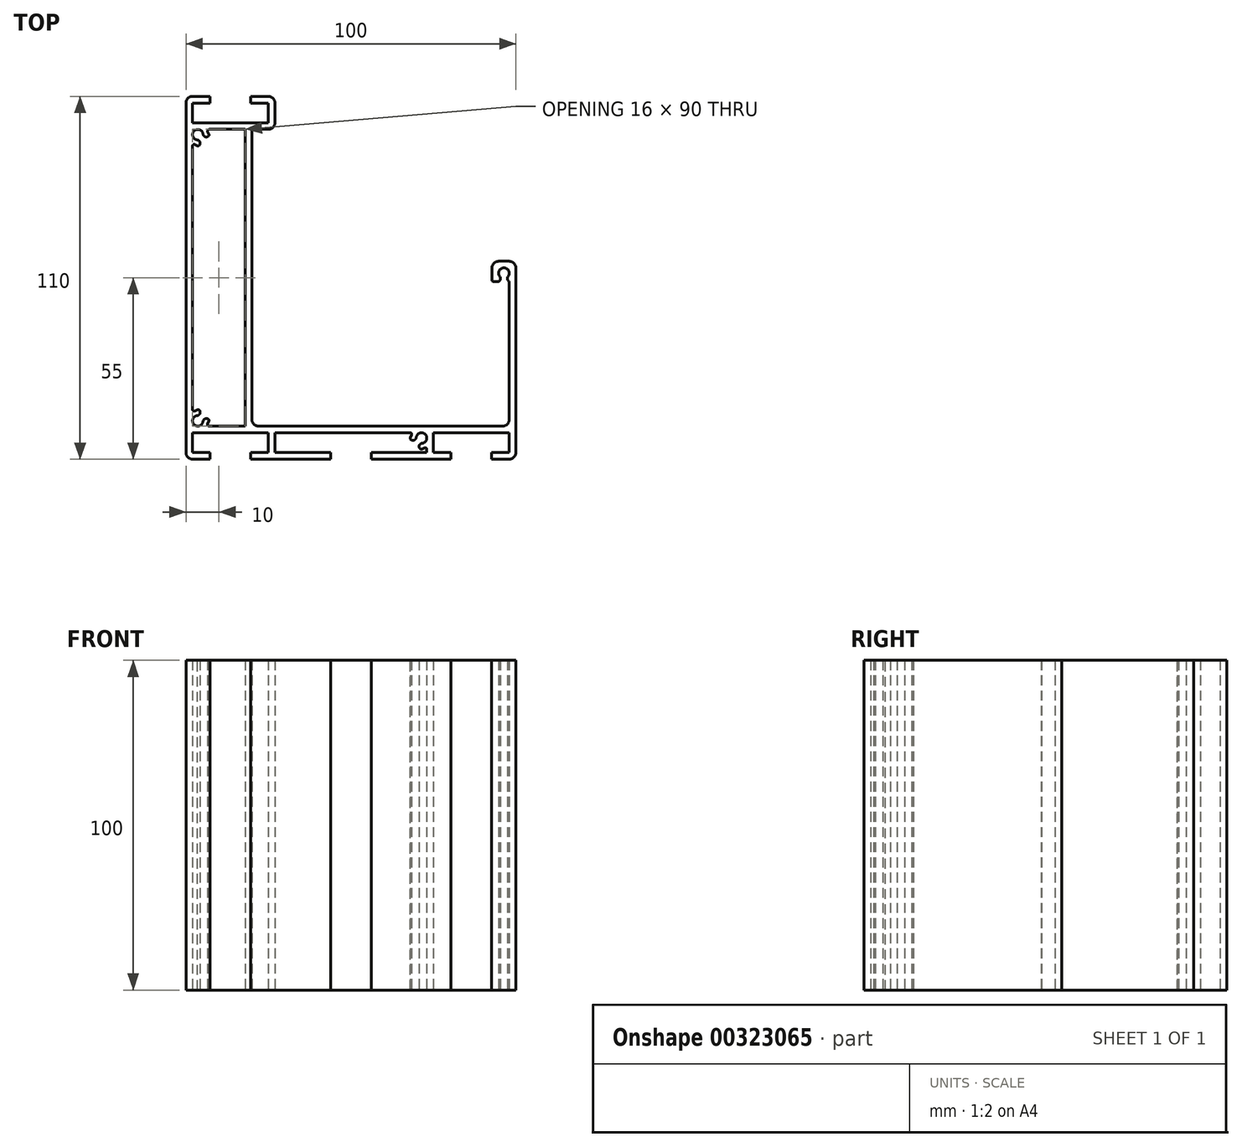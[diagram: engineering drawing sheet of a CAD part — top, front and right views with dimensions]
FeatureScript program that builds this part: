
annotation { "Feature Type Name" : "Feature", "Feature Type Description" : "" }
export const myFeature = defineFeature(function(context is Context, id is Id, definition is map)
    precondition{}
    {
        {
            var Q0;
            Q0=qCreatedBy(makeId("Top.planeOp"),FACE);
            var sketch = newSketch(context, id + "F0", { "sketchPlane" : qUnion([Q0])});
            skLineSegment(sketch, "E0", {"start": v(-2, 108) * mm, "end": v(-2, 2) * mm});
            skArc(sketch, "E1", {"start": v(0, 110) * mm, "mid": v(-1.41, 109.41) * mm, "end": v(-2, 108) * mm});
            skLineSegment(sketch, "E2", {"start": v(0, 108) * mm, "end": v(0, 102) * mm});
            skLineSegment(sketch, "E3", {"start": v(0, 94.94) * mm, "end": v(0, 15.06) * mm});
            skLineSegment(sketch, "E4", {"start": v(0, 8) * mm, "end": v(0, 2) * mm});
            skLineSegment(sketch, "E5", {"start": v(0, 0) * mm, "end": v(5.35, 0) * mm});
            skArc(sketch, "E6", {"start": v(-2, 2) * mm, "mid": v(-1.41, 0.59) * mm, "end": v(0, 0) * mm});
            skLineSegment(sketch, "E7", {"start": v(17.65, 0) * mm, "end": v(41.85, 0) * mm});
            skLineSegment(sketch, "E8", {"start": v(54.15, 0) * mm, "end": v(78.35, 0) * mm});
            skLineSegment(sketch, "E9", {"start": v(90.65, 0) * mm, "end": v(96, 0) * mm});
            skLineSegment(sketch, "E10", {"start": v(0, 2) * mm, "end": v(5.35, 2) * mm});
            skLineSegment(sketch, "E11", {"start": v(17.65, 2) * mm, "end": v(23, 2) * mm});
            skLineSegment(sketch, "E12", {"start": v(25, 2) * mm, "end": v(41.85, 2) * mm});
            skLineSegment(sketch, "E13", {"start": v(54.15, 2) * mm, "end": v(71, 2) * mm});
            skLineSegment(sketch, "E14", {"start": v(73, 2) * mm, "end": v(78.35, 2) * mm});
            skLineSegment(sketch, "E15", {"start": v(90.65, 2) * mm, "end": v(96, 2) * mm});
            skLineSegment(sketch, "E16", {"start": v(98, 2) * mm, "end": v(98, 58) * mm});
            skArc(sketch, "E17", {"start": v(98, 58) * mm, "mid": v(97.41, 59.41) * mm, "end": v(96, 60) * mm});
            skArc(sketch, "E18", {"start": v(96, 0) * mm, "mid": v(97.41, 0.59) * mm, "end": v(98, 2) * mm});
            skLineSegment(sketch, "E19", {"start": v(96, 2) * mm, "end": v(96, 8) * mm});
            skLineSegment(sketch, "E20", {"start": v(96, 12) * mm, "end": v(96, 53.87) * mm});
            skLineSegment(sketch, "E21", {"start": v(90.8, 54.28) * mm, "end": v(90.8, 58) * mm});
            skArc(sketch, "E22", {"start": v(90.8, 54.28) * mm, "mid": v(90.95, 53.92) * mm, "end": v(91.3, 53.78) * mm});
            skArc(sketch, "E23", {"start": v(94, 10) * mm, "mid": v(95.41, 10.59) * mm, "end": v(96, 12) * mm});
            skLineSegment(sketch, "E24", {"start": v(0, 110) * mm, "end": v(5.35, 110) * mm});
            skLineSegment(sketch, "E25", {"start": v(17.65, 110) * mm, "end": v(23, 110) * mm});
            skLineSegment(sketch, "E26", {"start": v(0, 108) * mm, "end": v(5.35, 108) * mm});
            skLineSegment(sketch, "E27", {"start": v(17.65, 108) * mm, "end": v(23, 108) * mm});
            skLineSegment(sketch, "E28", {"start": v(25, 108) * mm, "end": v(25, 102) * mm});
            skArc(sketch, "E29", {"start": v(25, 108) * mm, "mid": v(24.41, 109.41) * mm, "end": v(23, 110) * mm});
            skLineSegment(sketch, "E30", {"start": v(23, 108) * mm, "end": v(23, 102) * mm});
            skLineSegment(sketch, "E31", {"start": v(23, 100) * mm, "end": v(18, 100) * mm});
            skArc(sketch, "E32", {"start": v(23, 100) * mm, "mid": v(24.41, 100.59) * mm, "end": v(25, 102) * mm});
            skLineSegment(sketch, "E33", {"start": v(16, 100) * mm, "end": v(5.06, 100) * mm});
            skLineSegment(sketch, "E34", {"start": v(23, 102) * mm, "end": v(0, 102) * mm});
            skLineSegment(sketch, "E35", {"start": v(94, 10) * mm, "end": v(20, 10) * mm});
            skArc(sketch, "E36", {"start": v(18, 12) * mm, "mid": v(18.59, 10.59) * mm, "end": v(20, 10) * mm});
            skLineSegment(sketch, "E37", {"start": v(16, 10) * mm, "end": v(5.06, 10) * mm});
            skLineSegment(sketch, "E38", {"start": v(96, 8) * mm, "end": v(73, 8) * mm});
            skLineSegment(sketch, "E39", {"start": v(65.94, 8) * mm, "end": v(25, 8) * mm});
            skLineSegment(sketch, "E40", {"start": v(23, 8) * mm, "end": v(0, 8) * mm});
            skLineSegment(sketch, "E41", {"start": v(18, 12) * mm, "end": v(18, 100) * mm});
            skLineSegment(sketch, "E42", {"start": v(16, 10) * mm, "end": v(16, 100) * mm});
            skLineSegment(sketch, "E43", {"start": v(25, 8) * mm, "end": v(25, 2) * mm});
            skLineSegment(sketch, "E44", {"start": v(23, 8) * mm, "end": v(23, 2) * mm});
            skLineSegment(sketch, "E45", {"start": v(71, 2.94) * mm, "end": v(71, 2) * mm});
            skLineSegment(sketch, "E46", {"start": v(73, 8) * mm, "end": v(73, 2) * mm});
            skLineSegment(sketch, "E47", {"start": v(17.65, 110) * mm, "end": v(17.65, 108) * mm});
            skLineSegment(sketch, "E48", {"start": v(5.35, 110) * mm, "end": v(5.35, 108) * mm});
            skLineSegment(sketch, "E49", {"start": v(17.65, 2) * mm, "end": v(17.65, 0) * mm});
            skLineSegment(sketch, "E50", {"start": v(5.35, 2) * mm, "end": v(5.35, 0) * mm});
            skLineSegment(sketch, "E51", {"start": v(90.65, 2) * mm, "end": v(90.65, 0) * mm});
            skLineSegment(sketch, "E52", {"start": v(78.35, 2) * mm, "end": v(78.35, 0) * mm});
            skLineSegment(sketch, "E53", {"start": v(96, 60) * mm, "end": v(92.8, 60) * mm});
            skArc(sketch, "E54", {"start": v(92.8, 60) * mm, "mid": v(91.39, 59.41) * mm, "end": v(90.8, 58) * mm});
            skArc(sketch, "E55", {"start": v(3.2, 98.57) * mm, "mid": v(0.47, 99.53) * mm, "end": v(1.43, 96.8) * mm});
            skLineSegment(sketch, "E56", {"start": v(4.6, 99.3) * mm, "end": v(4.96, 98.51) * mm});
            skArc(sketch, "E57", {"start": v(5.06, 100) * mm, "mid": v(4.64, 99.77) * mm, "end": v(4.6, 99.3) * mm});
            skArc(sketch, "E58", {"start": v(4.82, 97.92) * mm, "mid": v(5, 98.2) * mm, "end": v(4.96, 98.51) * mm});
            skArc(sketch, "E59", {"start": v(3.2, 98.58) * mm, "mid": v(3.81, 97.76) * mm, "end": v(4.82, 97.92) * mm});
            skArc(sketch, "E60", {"start": v(2.08, 95.18) * mm, "mid": v(2.24, 96.19) * mm, "end": v(1.42, 96.8) * mm});
            skArc(sketch, "E61", {"start": v(1.5, 95.04) * mm, "mid": v(1.81, 95.01) * mm, "end": v(2.08, 95.18) * mm});
            skLineSegment(sketch, "E62", {"start": v(1.5, 95.04) * mm, "end": v(0.7, 95.4) * mm});
            skLineSegment(sketch, "E63", {"start": v(5.06, 100) * mm, "end": v(6.06, 100) * mm});
            skLineSegment(sketch, "E64", {"start": v(0, 86.97) * mm, "end": v(0, 85.72) * mm});
            skArc(sketch, "E65", {"start": v(0.7, 95.4) * mm, "mid": v(0.23, 95.36) * mm, "end": v(0, 94.94) * mm});
            skArc(sketch, "E66", {"start": v(1.43, 13.2) * mm, "mid": v(0.47, 10.47) * mm, "end": v(3.2, 11.43) * mm});
            skLineSegment(sketch, "E67", {"start": v(4.6, 10.7) * mm, "end": v(4.96, 11.49) * mm});
            skArc(sketch, "E68", {"start": v(4.6, 10.7) * mm, "mid": v(4.64, 10.23) * mm, "end": v(5.06, 10) * mm});
            skArc(sketch, "E69", {"start": v(4.96, 11.49) * mm, "mid": v(5, 11.8) * mm, "end": v(4.82, 12.08) * mm});
            skArc(sketch, "E70", {"start": v(4.82, 12.08) * mm, "mid": v(3.81, 12.24) * mm, "end": v(3.2, 11.42) * mm});
            skArc(sketch, "E71", {"start": v(1.42, 13.2) * mm, "mid": v(2.24, 13.81) * mm, "end": v(2.08, 14.82) * mm});
            skArc(sketch, "E72", {"start": v(2.08, 14.82) * mm, "mid": v(1.81, 14.99) * mm, "end": v(1.5, 14.96) * mm});
            skLineSegment(sketch, "E73", {"start": v(1.5, 14.96) * mm, "end": v(0.7, 14.6) * mm});
            skArc(sketch, "E74", {"start": v(0, 15.06) * mm, "mid": v(0.23, 14.64) * mm, "end": v(0.7, 14.6) * mm});
            skArc(sketch, "E75", {"start": v(69.57, 4.8) * mm, "mid": v(70.53, 7.53) * mm, "end": v(67.8, 6.57) * mm});
            skLineSegment(sketch, "E76", {"start": v(70.3, 3.4) * mm, "end": v(69.51, 3.04) * mm});
            skArc(sketch, "E77", {"start": v(71, 2.94) * mm, "mid": v(70.77, 3.36) * mm, "end": v(70.3, 3.4) * mm});
            skArc(sketch, "E78", {"start": v(68.92, 3.18) * mm, "mid": v(69.2, 3) * mm, "end": v(69.51, 3.04) * mm});
            skArc(sketch, "E79", {"start": v(69.58, 4.8) * mm, "mid": v(68.76, 4.19) * mm, "end": v(68.92, 3.18) * mm});
            skArc(sketch, "E80", {"start": v(66.18, 5.92) * mm, "mid": v(67.19, 5.76) * mm, "end": v(67.8, 6.58) * mm});
            skArc(sketch, "E81", {"start": v(66.04, 6.5) * mm, "mid": v(66.01, 6.19) * mm, "end": v(66.18, 5.92) * mm});
            skLineSegment(sketch, "E82", {"start": v(66.04, 6.5) * mm, "end": v(66.4, 7.3) * mm});
            skArc(sketch, "E83", {"start": v(66.4, 7.3) * mm, "mid": v(66.36, 7.77) * mm, "end": v(65.94, 8) * mm});
            skArc(sketch, "E84", {"start": v(95.65, 55.4) * mm, "mid": v(94.4, 58) * mm, "end": v(93.15, 55.4) * mm});
            skArc(sketch, "E85", {"start": v(95.65, 55.4) * mm, "mid": v(95.46, 54.55) * mm, "end": v(96, 53.87) * mm});
            skArc(sketch, "E86", {"start": v(92.37, 53.78) * mm, "mid": v(93.27, 54.34) * mm, "end": v(93.15, 55.4) * mm});
            skLineSegment(sketch, "E87", {"start": v(92.37, 53.78) * mm, "end": v(91.3, 53.78) * mm});
            skLineSegment(sketch, "E88", {"start": v(41.85, 2) * mm, "end": v(41.85, 0) * mm});
            skLineSegment(sketch, "E89", {"start": v(54.15, 2) * mm, "end": v(54.15, 0) * mm});
            skSolve(sketch);
        }
        {
            var Q0;
            Q0 = qSketchRegion(id + "F0", true);
            extrude(context, id + "F1", {"entities" : qUnion([Q0]), "endBound" : BoundingType.SYMMETRIC, "depth" : 100 * mm});
        }
    });
